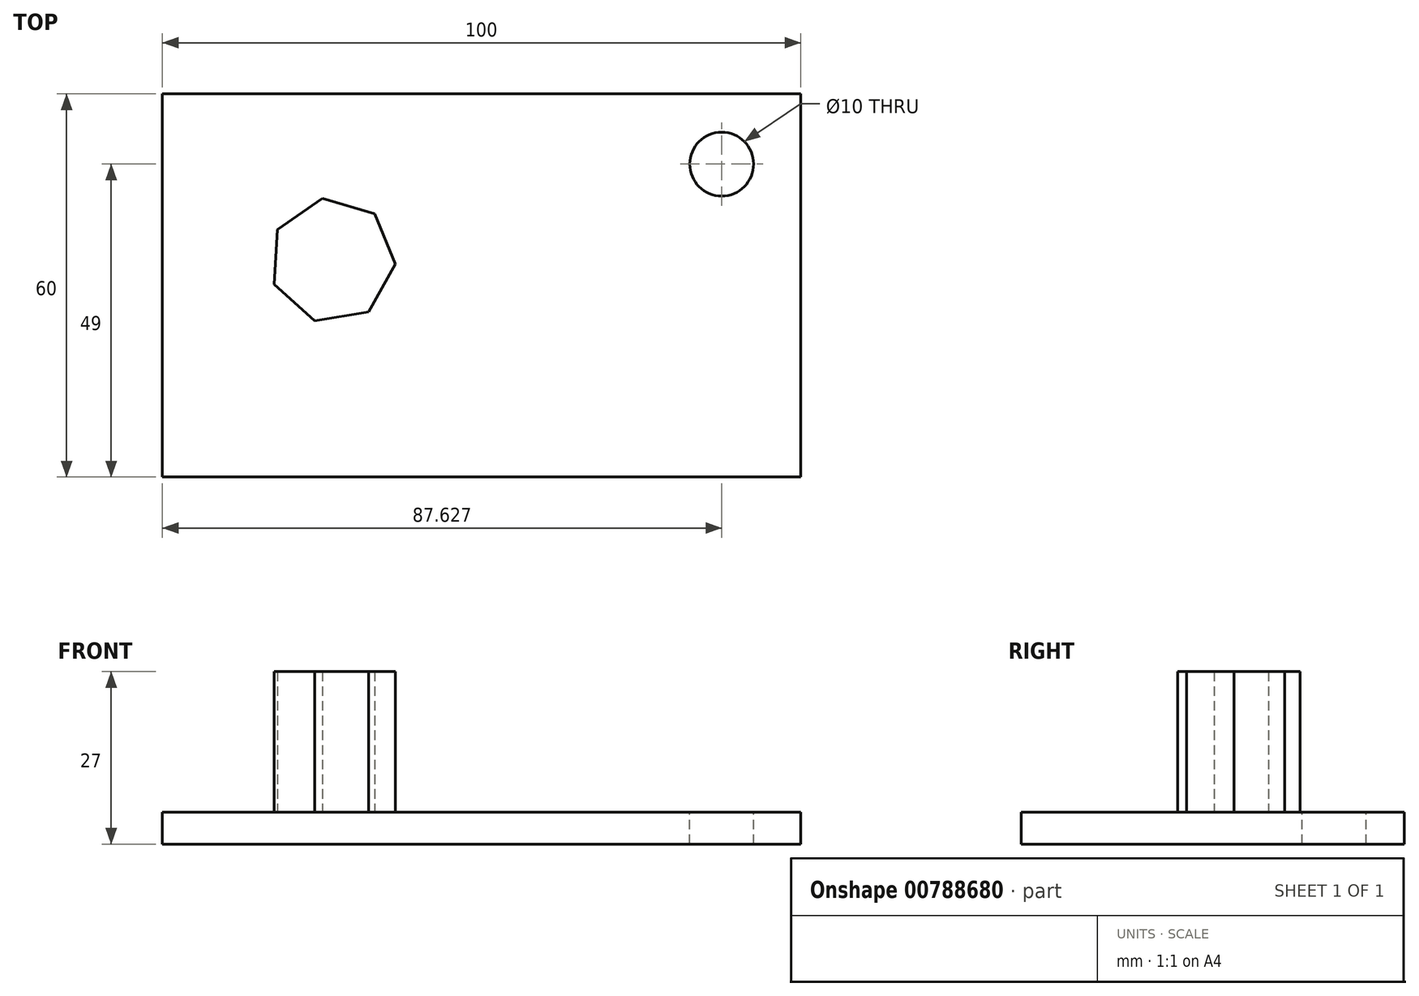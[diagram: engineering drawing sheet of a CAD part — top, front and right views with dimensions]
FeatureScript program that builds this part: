
annotation { "Feature Type Name" : "Feature", "Feature Type Description" : "" }
export const myFeature = defineFeature(function(context is Context, id is Id, definition is map)
    precondition{}
    {
        {
            var Q0;
            Q0=qCreatedBy(makeId("Top.planeOp"),FACE);
            var sketch = newSketch(context, id + "F0", { "sketchPlane" : qUnion([Q0])});
            skPoint(sketch, "E0.middle", {"position": v(0, 0) * mm});
            skLineSegment(sketch, "E1.bottom", {"start": v(50, 30) * mm, "end": v(-50, 30) * mm});
            skLineSegment(sketch, "E1.top", {"start": v(50, -30) * mm, "end": v(-50, -30) * mm});
            skLineSegment(sketch, "E1.left", {"start": v(50, 30) * mm, "end": v(50, -30) * mm});
            skLineSegment(sketch, "E1.right", {"start": v(-50, 30) * mm, "end": v(-50, -30) * mm});
            skSolve(sketch);
        }
        {
            var Q0;
            Q0 = qSketchRegion(id + "F0", true);
            extrude(context, id + "F1", {"entities" : qUnion([Q0]), "depth" : 5 * mm, "offsetDistance" : 25 * mm});
        }
        {
            var Q0;
            Q0=makeQuery(id+"F1.opExtrude","CAP_FACE",FACE,{"disambiguationData":[OSD([sQuery(id+"F0.wireOp",EDGE,"E1.bottom"),sQuery(id+"F0.wireOp",EDGE,"E1.top"),sQuery(id+"F0.wireOp",EDGE,"E1.left"),sQuery(id+"F0.wireOp",EDGE,"E1.right")])],"isStart":false});
            var sketch = newSketch(context, id + "F2", { "sketchPlane" : qUnion([Q0])});
            skCircle(sketch, "E2", {"center": v(37.63, 19) * mm, "radius": 5 * mm});
            skSolve(sketch);
        }
        {
            var Q0;
            Q0=makeQuery(id+"F2.imprint","IMPRINT",FACE,{"disambiguationData":[TD([[makeQuery(id+"F2.imprint","IMPRINT",EDGE,{"derivedFrom":sQuery(id+"F2.wireOp",EDGE,"E2")}),1.0]])]});
            extrude(context, id + "F3", {"entities" : qUnion([Q0]), "operationType" : NewBodyOperationType.REMOVE, "oppositeDirection" : true, "depth" : 25 * mm, "offsetDistance" : 25 * mm});
        }
        {
            var Q0;
            Q0=makeQuery(id+"F1.opExtrude","CAP_FACE",FACE,{"disambiguationData":[OSD([sQuery(id+"F0.wireOp",EDGE,"E1.bottom"),sQuery(id+"F0.wireOp",EDGE,"E1.top"),sQuery(id+"F0.wireOp",EDGE,"E1.left"),sQuery(id+"F0.wireOp",EDGE,"E1.right")])],"isStart":false});
            var sketch = newSketch(context, id + "F4", { "sketchPlane" : qUnion([Q0])});
            skCircle(sketch, "E3.cCircle", {"center": v(-23.34, 3.92) * mm, "radius": 8.88 * mm, "construction": true});
            skLineSegment(sketch, "E3.0", {"start": v(-16.74, 11.24) * mm, "end": v(-13.5, 3.33) * mm});
            skLineSegment(sketch, "E3.1", {"start": v(-13.5, 3.33) * mm, "end": v(-17.68, -4.14) * mm});
            skLineSegment(sketch, "E3.2", {"start": v(-17.68, -4.14) * mm, "end": v(-26.11, -5.53) * mm});
            skLineSegment(sketch, "E3.3", {"start": v(-26.11, -5.53) * mm, "end": v(-32.46, 0.2) * mm});
            skLineSegment(sketch, "E3.4", {"start": v(-32.46, 0.2) * mm, "end": v(-31.95, 8.73) * mm});
            skLineSegment(sketch, "E3.5", {"start": v(-31.95, 8.73) * mm, "end": v(-24.95, 13.64) * mm});
            skLineSegment(sketch, "E3.6", {"start": v(-24.95, 13.64) * mm, "end": v(-16.74, 11.24) * mm});
            skPoint(sketch, "E3.0.midPoint", {"position": v(-15.13, 7.28) * mm});
            skSolve(sketch);
        }
        {
            var Q0;
            Q0=makeQuery(id+"F4.imprint","IMPRINT",FACE,{"disambiguationData":[TD([[makeQuery(id+"F4.imprint","IMPRINT",EDGE,{"derivedFrom":sQuery(id+"F4.wireOp",EDGE,"E3.0")}),-1.0]])]});
            extrude(context, id + "F5", {"entities" : qUnion([Q0]), "operationType" : NewBodyOperationType.ADD, "depth" : 22 * mm, "offsetDistance" : 25 * mm});
        }
    });
